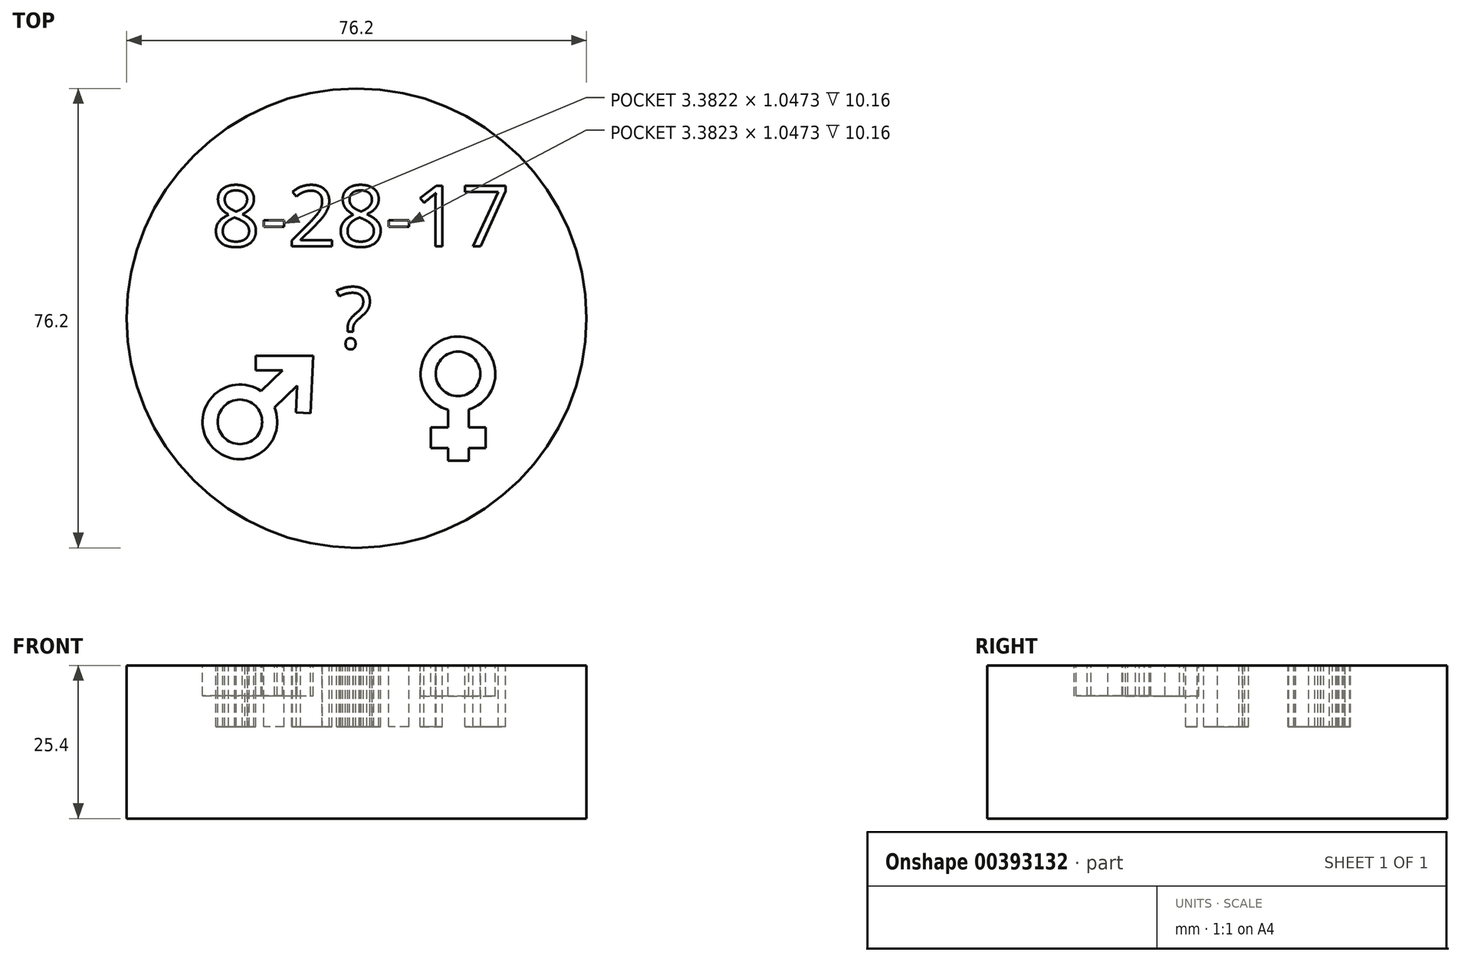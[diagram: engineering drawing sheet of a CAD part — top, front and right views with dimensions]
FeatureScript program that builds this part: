
annotation { "Feature Type Name" : "Feature", "Feature Type Description" : "" }
export const myFeature = defineFeature(function(context is Context, id is Id, definition is map)
    precondition{}
    {
        {
            var Q0;
            Q0=qCreatedBy(makeId("Top.planeOp"),FACE);
            var sketch = newSketch(context, id + "F0", { "sketchPlane" : qUnion([Q0])});
            skCircle(sketch, "E0", {"center": v(0, 0) * mm, "radius": 38.1 * mm});
            skSolve(sketch);
        }
        {
            var Q0;
            Q0=qCreatedBy(makeId("Top.planeOp"),FACE);
            var sketch = newSketch(context, id + "F1", { "sketchPlane" : qUnion([Q0])});
            skText(sketch, "E1", { "text": "8-28-17", "fontName": "OpenSans-Regular.ttf"});
            skText(sketch, "E2", { "text": "?", "fontName": "OpenSans-Regular.ttf"});
            skCircle(sketch, "E3", {"center": v(-19.31, -17.21) * mm, "radius": 3.69 * mm});
            skCircle(sketch, "E4", {"center": v(-19.31, -17.21) * mm, "radius": 6.19 * mm});
            skLineSegment(sketch, "E5", {"start": v(-15.83, -12.1) * mm, "end": v(-12.24, -8.67) * mm});
            skLineSegment(sketch, "E6", {"start": v(-13.6, -14.82) * mm, "end": v(-9.62, -11.03) * mm});
            skLineSegment(sketch, "E7", {"start": v(-12.24, -8.67) * mm, "end": v(-16.7, -8.67) * mm});
            skLineSegment(sketch, "E8", {"start": v(-16.7, -8.67) * mm, "end": v(-16.7, -6.25) * mm});
            skLineSegment(sketch, "E9", {"start": v(-16.7, -6.25) * mm, "end": v(-7.15, -6.25) * mm});
            skLineSegment(sketch, "E10.MirrorCS", {"start": v(-7.62, -15.78) * mm, "end": v(-7.15, -6.25) * mm});
            skLineSegment(sketch, "E11.MirrorCS", {"start": v(-9.82, -11.22) * mm, "end": v(-10.04, -15.66) * mm});
            skLineSegment(sketch, "E12.MirrorCS", {"start": v(-10.04, -15.66) * mm, "end": v(-7.62, -15.78) * mm});
            skCircle(sketch, "E13", {"center": v(16.82, -9.24) * mm, "radius": 3.69 * mm});
            skCircle(sketch, "E14", {"center": v(16.82, -9.24) * mm, "radius": 6.19 * mm});
            skLineSegment(sketch, "E15", {"start": v(18.64, -15.16) * mm, "end": v(18.64, -23.67) * mm});
            skLineSegment(sketch, "E16", {"start": v(15.18, -15.2) * mm, "end": v(15.18, -23.67) * mm});
            skLineSegment(sketch, "E17", {"start": v(15.18, -23.67) * mm, "end": v(18.64, -23.67) * mm});
            skLineSegment(sketch, "E18", {"start": v(18.64, -21.55) * mm, "end": v(21.43, -21.55) * mm});
            skLineSegment(sketch, "E19", {"start": v(21.43, -21.55) * mm, "end": v(21.43, -18.14) * mm});
            skLineSegment(sketch, "E20", {"start": v(21.43, -18.14) * mm, "end": v(12.3, -18.14) * mm});
            skLineSegment(sketch, "E21", {"start": v(12.3, -18.14) * mm, "end": v(12.3, -21.55) * mm});
            skLineSegment(sketch, "E22", {"start": v(12.3, -21.55) * mm, "end": v(15.18, -21.55) * mm});
            const initialGuessF1  = {"E1": [-0.024, 0.01189, 1, 0, 0.01016], "E2": [-0.00346, -0.005, 1, 0, 0.01016]};
            skSetInitialGuess(sketch, initialGuessF1);
            skSolve(sketch);
        }
        {
            var Q0;
            Q0=makeQuery(id+"F0.imprint","IMPRINT",FACE,{"disambiguationData":[TD([[makeQuery(id+"F0.imprint","IMPRINT",EDGE,{"derivedFrom":sQuery(id+"F0.wireOp",EDGE,"E0")}),1.0]])]});
            extrude(context, id + "F2", {"entities" : qUnion([Q0]), "offsetDistance" : 25.4 * mm, "depth" : -25.4 * mm});
        }
        {
            var Q0;
            Q0=makeQuery(id+"F1.imprint","IMPRINT",FACE,{"disambiguationData":[TD([[makeQuery(id+"F1.imprint","IMPRINT",EDGE,{"derivedFrom":sQuery(id+"F1.wireOp",EDGE,"E3")}),-1.0]])]});
            var Q1;
            {var subQ4=sQuery(id+"F1.wireOp",EDGE,"E5");Q1=makeQuery(id+"F1.imprint","IMPRINT",FACE,{"disambiguationData":[TD([[makeQuery(id+"F1.imprint","IMPRINT",EDGE,{"derivedFrom":subQ4}),-1.0]])]});}
            extrude(context, id + "F3", {"entities" : qUnion([Q0, Q1]), "operationType" : NewBodyOperationType.REMOVE, "oppositeDirection" : true, "offsetDistance" : 25.4 * mm, "depth" : 5.03 * mm});
        }
        {
            var Q0;
            Q0=makeQuery(id+"F1.imprint","IMPRINT",FACE,{"disambiguationData":[TD([[makeQuery(id+"F1.imprint","IMPRINT",EDGE,{"derivedFrom":sQuery(id+"F1.wireOp",EDGE,"E13")}),-1.0]])]});
            var Q1;
            {var subQ0=sQuery(id+"F1.wireOp",EDGE,"E15");Q1=makeQuery(id+"F1.imprint","IMPRINT",FACE,{"disambiguationData":[TD([[makeQuery(id+"F1.imprint","IMPRINT",EDGE,{"derivedFrom":subQ0}),-1.0]])]});}
            var Q2;
            {var subQ0=sQuery(id+"F1.wireOp",EDGE,"E15");var subQ1=sQuery(id+"F1.wireOp",EDGE,"E14");var subQ2=makeQuery(id+"F1.imprint","INTERSECT",VERTEX,{"derivedFrom":[subQ1,subQ0]});Q2=makeQuery(id+"F1.imprint","IMPRINT",FACE,{"disambiguationData":[TD([[makeQuery(id+"F1.imprint","IMPRINT",EDGE,{"disambiguationData":[TD([[subQ2,1.0]])],"derivedFrom":subQ1}),-1.0]])]});}
            var Q3;
            {var subQ0=sQuery(id+"F1.wireOp",EDGE,"E18");Q3=makeQuery(id+"F1.imprint","IMPRINT",FACE,{"disambiguationData":[TD([[makeQuery(id+"F1.imprint","IMPRINT",EDGE,{"derivedFrom":subQ0}),1.0]])]});}
            var Q4;
            {var subQ4=sQuery(id+"F1.wireOp",EDGE,"E21");Q4=makeQuery(id+"F1.imprint","IMPRINT",FACE,{"disambiguationData":[TD([[makeQuery(id+"F1.imprint","IMPRINT",EDGE,{"derivedFrom":subQ4}),1.0]])]});}
            extrude(context, id + "F4", {"entities" : qUnion([Q0, Q1, Q2, Q3, Q4]), "operationType" : NewBodyOperationType.REMOVE, "oppositeDirection" : true, "offsetDistance" : 25.4 * mm, "depth" : 5.08 * mm});
        }
        {
            var Q0;
            Q0=makeQuery(id+"F1.imprint","IMPRINT",FACE,{"disambiguationData":[TD([[makeQuery(id+"F1.imprint","IMPRINT",EDGE,{"derivedFrom":sQuery(id+"F1.wireOp",EDGE,"E1.sketch_text.stroke-31")}),-1.0]])]});
            var Q1;
            Q1=makeQuery(id+"F1.imprint","IMPRINT",FACE,{"disambiguationData":[TD([[makeQuery(id+"F1.imprint","IMPRINT",EDGE,{"derivedFrom":sQuery(id+"F1.wireOp",EDGE,"E1.sketch_text.stroke-35")}),-1.0]])]});
            var Q2;
            Q2=makeQuery(id+"F1.imprint","IMPRINT",FACE,{"disambiguationData":[TD([[makeQuery(id+"F1.imprint","IMPRINT",EDGE,{"derivedFrom":sQuery(id+"F1.wireOp",EDGE,"E1.sketch_text.stroke-55")}),-1.0]])]});
            var Q3;
            Q3=makeQuery(id+"F1.imprint","IMPRINT",FACE,{"disambiguationData":[TD([[makeQuery(id+"F1.imprint","IMPRINT",EDGE,{"derivedFrom":sQuery(id+"F1.wireOp",EDGE,"E1.sketch_text.stroke-0")}),-1.0]])]});
            var Q4;
            Q4=makeQuery(id+"F1.imprint","IMPRINT",FACE,{"disambiguationData":[TD([[makeQuery(id+"F1.imprint","IMPRINT",EDGE,{"derivedFrom":sQuery(id+"F1.wireOp",EDGE,"E1.sketch_text.stroke-86")}),-1.0]])]});
            var Q5;
            Q5=makeQuery(id+"F1.imprint","IMPRINT",FACE,{"disambiguationData":[TD([[makeQuery(id+"F1.imprint","IMPRINT",EDGE,{"derivedFrom":sQuery(id+"F1.wireOp",EDGE,"E1.sketch_text.stroke-90")}),-1.0]])]});
            var Q6;
            Q6=makeQuery(id+"F1.imprint","IMPRINT",FACE,{"disambiguationData":[TD([[makeQuery(id+"F1.imprint","IMPRINT",EDGE,{"derivedFrom":sQuery(id+"F1.wireOp",EDGE,"E1.sketch_text.stroke-99")}),-1.0]])]});
            var Q7;
            Q7=makeQuery(id+"F1.imprint","IMPRINT",FACE,{"disambiguationData":[TD([[makeQuery(id+"F1.imprint","IMPRINT",EDGE,{"derivedFrom":sQuery(id+"F1.wireOp",EDGE,"E2.sketch_text.stroke-0")}),-1.0]])]});
            var Q8;
            Q8=makeQuery(id+"F1.imprint","IMPRINT",FACE,{"disambiguationData":[TD([[makeQuery(id+"F1.imprint","IMPRINT",EDGE,{"derivedFrom":sQuery(id+"F1.wireOp",EDGE,"E2.sketch_text.stroke-20")}),-1.0]])]});
            extrude(context, id + "F5", {"entities" : qUnion([Q0, Q1, Q2, Q3, Q4, Q5, Q6, Q7, Q8]), "operationType" : NewBodyOperationType.REMOVE, "oppositeDirection" : true, "depth" : 10.16 * mm});
        }
    });
